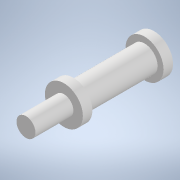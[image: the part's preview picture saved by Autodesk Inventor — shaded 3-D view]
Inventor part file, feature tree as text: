
AUTODESK INVENTOR PART (.ipt)
format: ipt  version: 2022 (Build 260153000, 153)  size: 125,952 bytes
history: native  units: mm
features: extrude x5, sketch x5, other x3, reference x3
ambient origin geometry x8: Origin, YZ Plane, XZ Plane, XY Plane, X Axis, Y Axis, Z Axis, Center Point
bodies: Body1 (feature_tree)
feature tree (16):
  other  "Твердое тело1"
  extrude  "Выдавливание1"  Depth=15.0mm TaperAngle=0.0deg
  extrude  "Выдавливание2"  Depth=8.0mm
  extrude  "Выдавливание3"  Depth=2.0mm TaperAngle=0.0deg
  extrude  "Выдавливание4"  Depth=4.0mm
  extrude  "Выдавливание5"  Depth=5.5mm
  sketch  "Эскиз1"
  reference  "Ссылка1"
  sketch  "Эскиз2"
  reference  "Ссылка2"
  sketch  "Эскиз3"
  reference  "Ссылка3"
  sketch  "Эскиз4"
  sketch  "Эскиз5"
  other  "Сборка2"
  other  "top:1"
